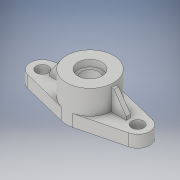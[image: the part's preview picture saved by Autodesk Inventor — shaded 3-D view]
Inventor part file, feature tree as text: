
AUTODESK INVENTOR PART (.ipt)
format: ipt  version: 2018 (Build 220112000, 112)  size: 199,680 bytes
history: native  units: mm
features: extrude x8, sketch x5
ambient origin geometry x8: Origin, YZ Plane, XZ Plane, XY Plane, X Axis, Y Axis, Z Axis, Center Point
bodies: Solid1 (feature_tree)
feature tree (13):
  sketch  "Sketch1"  dims[d0=21.5mm d1=11.0mm]
  extrude  "Extrusion1"  Depth=11.0mm
  extrude  "Extrusion2"  Depth=21.75mm
  extrude  "Extrusion3"  Depth=5.5mm
  sketch  "Sketch2"  dims[d2=21.75mm d3=21.75mm]
  extrude  "Extrusion4"  Depth=5.5mm
  sketch  "Sketch3"  dims[d4=8.0mm d5=5.5mm]
  sketch  "Sketch4"  dims[d6=5.5mm d7=5.5mm]
  extrude  "Extrusion5"  Depth=5.5mm
  extrude  "Extrusion6"  TaperAngle=180.0deg  [1 undecoded]
  extrude  "Extrusion7"  Depth=5.5mm TaperAngle=0.0deg
  extrude  "Extrusion8"  Depth=13.5mm TaperAngle=0.0deg
  sketch  "Sketch5"  dims[d8=180.0deg d9=5.5mm d10=180.0deg d11=5.5mm d12=0.0mm d13=13.5mm d14=0.0mm d15=16.5mm d16=0.0mm d20=7.0mm d21=7.0mm d22=2.0mm d23=0.0mm d24=2.0mm d25=10.5mm d26=10.5mm d27=9.5mm d28=0.0mm d29=9.5mm d30=2.0mm d33=1.5mm d34=0.0mm d35=1.5mm d36=0.0mm d37=1.5mm d38=0.0mm d39=2.0mm d40=0.0mm]
note: 1 required parameter value undecoded (feature->parameter linkage not recoverable at this tier; creation-order binding heuristic only, values carry confidence <= 0.55)
